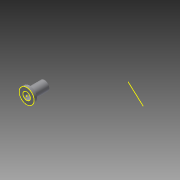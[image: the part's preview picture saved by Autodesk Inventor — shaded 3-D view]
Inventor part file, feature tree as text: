
AUTODESK INVENTOR PART (.ipt)
format: ipt  version: 2014 SP1 (Build 180222100, 222)  size: 76,288 bytes
history: native  units: in
note: dims shown in document units (in); Inventor stores cm internally (conversion verified against a paired STEP export)
features: other x2, sketch x1, imported_body x1, reference x1
ambient origin geometry x8: Origin, YZ Plane, XZ Plane, XY Plane, X Axis, Y Axis, Z Axis, Center Point
bodies: Body1 (feature_tree)
feature tree (5):
  other  "Boss-Extrude2"
  other  "AM-2235 threaded insert1"
  sketch  "Sketch1"
  imported_body  "Base1"
  reference  "Reference1"
